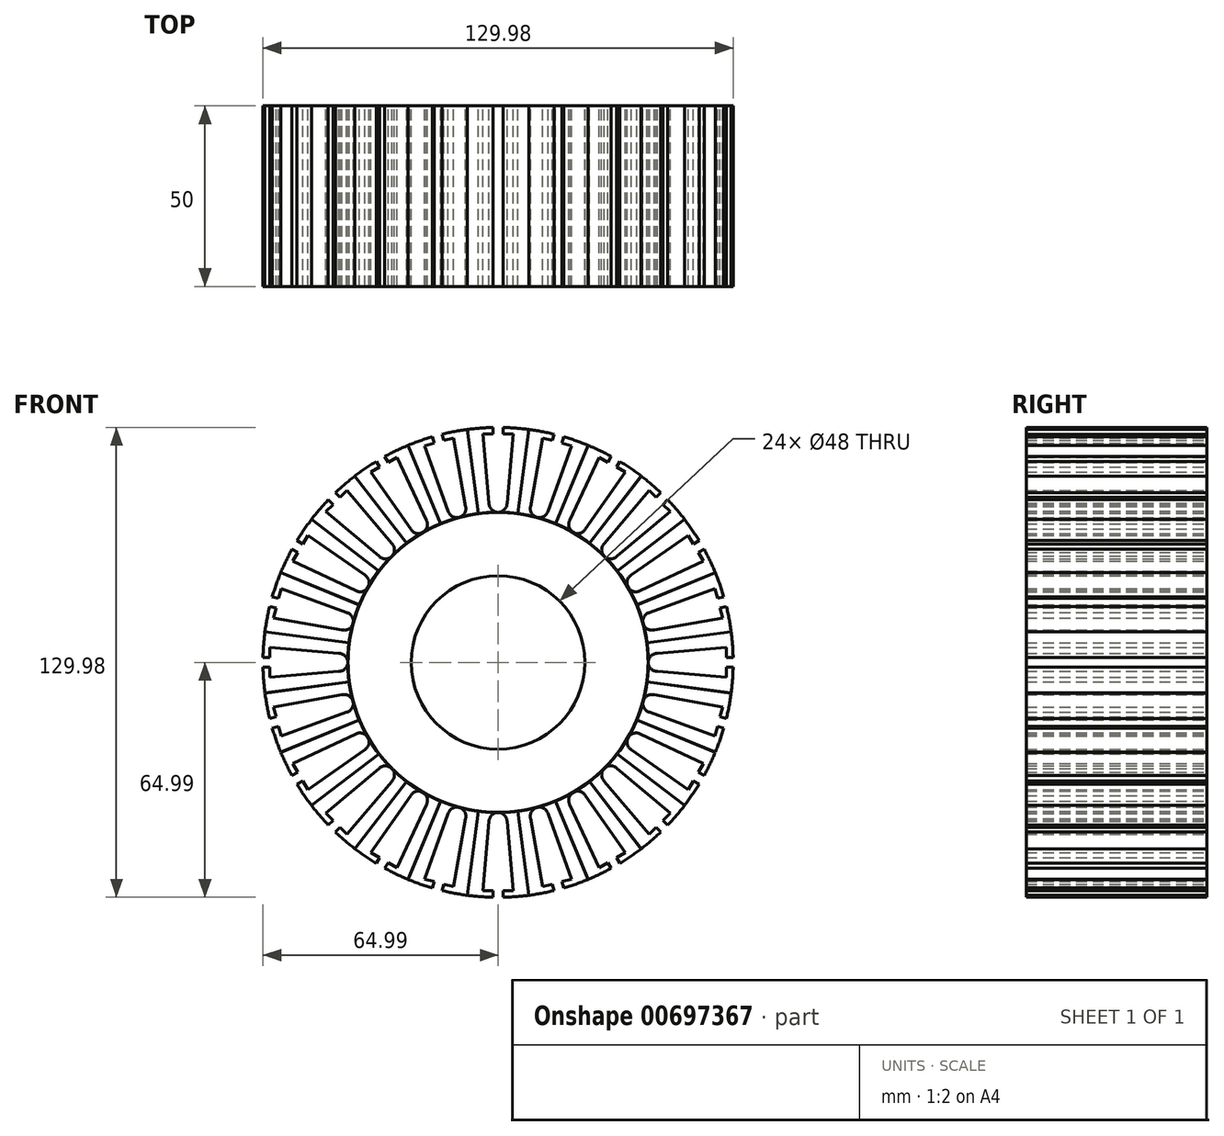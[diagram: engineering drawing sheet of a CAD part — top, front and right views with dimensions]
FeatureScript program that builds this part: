
annotation { "Feature Type Name" : "Feature", "Feature Type Description" : "" }
export const myFeature = defineFeature(function(context is Context, id is Id, definition is map)
    precondition{}
    {
        {
            var Q0;
            Q0=qCreatedBy(makeId("Front.planeOp"),FACE);
            var sketch = newSketch(context, id + "F0", { "sketchPlane" : qUnion([Q0])});
            skArc(sketch, "E0", {"start": v(-5.42, 41.18) * mm, "mid": v(0, -41.53) * mm, "end": v(5.42, 41.18) * mm});
            skArc(sketch, "E1", {"start": v(-2.49, 44.02) * mm, "mid": v(0, 41.53) * mm, "end": v(2.49, 44.02) * mm});
            skLineSegment(sketch, "E2", {"start": v(1.37, 63.16) * mm, "end": v(4.15, 63.16) * mm});
            skLineSegment(sketch, "E3", {"start": v(-1.37, 63.16) * mm, "end": v(-1.37, 64.99) * mm});
            skLineSegment(sketch, "E4.MirrorCS", {"start": v(1.37, 63.16) * mm, "end": v(1.37, 64.99) * mm});
            skLineSegment(sketch, "E5.MirrorCS", {"start": v(-1.37, 63.16) * mm, "end": v(-4.15, 63.16) * mm});
            skLineSegment(sketch, "E6", {"start": v(4.15, 63.16) * mm, "end": v(2.49, 44.02) * mm});
            skLineSegment(sketch, "E7", {"start": v(-2.49, 44.02) * mm, "end": v(-4.15, 63.16) * mm});
            skLineSegment(sketch, "E8", {"start": v(5.42, 41.18) * mm, "end": v(8.48, 64.44) * mm});
            skLineSegment(sketch, "E9", {"start": v(-5.42, 41.18) * mm, "end": v(-8.48, 64.44) * mm});
            skCircle(sketch, "E10", {"center": v(0, 0) * mm, "radius": 24 * mm});
            skArc(sketch, "E11", {"start": v(-1.38, 64.99) * mm, "mid": v(-4.93, 64.81) * mm, "end": v(-8.48, 64.44) * mm});
            skArc(sketch, "E12.trimOffspring", {"start": v(8.48, 64.44) * mm, "mid": v(4.93, 64.81) * mm, "end": v(1.37, 64.99) * mm});
            skSolve(sketch);
        }
        {
            var Q0;
            Q0=qSketchRegion(id+"F0",true);
            extrude(context, id + "F1", {"entities" : qUnion([Q0]), "depth" : 50 * mm, "offsetDistance" : 25 * mm});
        }
        {
            var Q0;
            Q0=makeQuery(id+"F1.opExtrude","SWEPT_BODY",BODY,{"disambiguationData":[OSD([sQuery(id+"F0.wireOp",EDGE,"E0"),sQuery(id+"F0.wireOp",EDGE,"E1"),sQuery(id+"F0.wireOp",EDGE,"E2"),sQuery(id+"F0.wireOp",EDGE,"E3"),sQuery(id+"F0.wireOp",EDGE,"E4.MirrorCS"),sQuery(id+"F0.wireOp",EDGE,"E5.MirrorCS"),sQuery(id+"F0.wireOp",EDGE,"E6"),sQuery(id+"F0.wireOp",EDGE,"E7"),sQuery(id+"F0.wireOp",EDGE,"E8"),sQuery(id+"F0.wireOp",EDGE,"E9"),sQuery(id+"F0.wireOp",EDGE,"E10"),sQuery(id+"F0.wireOp",EDGE,"E11"),sQuery(id+"F0.wireOp",EDGE,"E12.trimOffspring")])]});
            var Q1;
            Q1=makeQuery(id+"F1.opExtrude","SWEPT_FACE",FACE,{"disambiguationData":[OSD([sQuery(id+"F0.wireOp",EDGE,"E0")])]});
            circularPattern(context, id + "F2", {"entities" : qUnion([Q0]), "axis" : qUnion([Q1]), "angle" : 360 * degree, "instanceCount" : 24, "equalSpace" : true});
        }
    });
